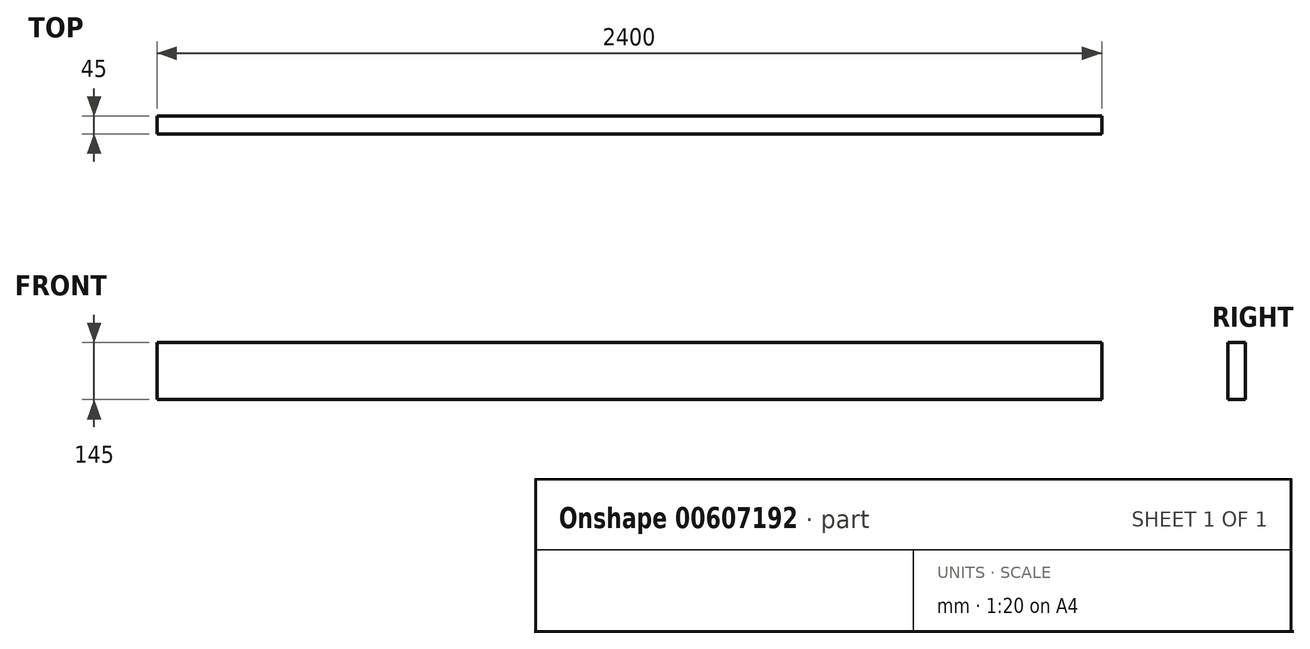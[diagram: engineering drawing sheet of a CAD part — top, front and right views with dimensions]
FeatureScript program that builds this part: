
annotation { "Feature Type Name" : "Feature", "Feature Type Description" : "" }
export const myFeature = defineFeature(function(context is Context, id is Id, definition is map)
    precondition{}
    {
        {
            var Q0;
            Q0=qCreatedBy(makeId("Front.planeOp"),FACE);
            var sketch = newSketch(context, id + "F0", { "sketchPlane" : qUnion([Q0])});
            skLineSegment(sketch, "E0.bottom", {"start": v(0, 0) * mm, "end": v(2400, 0) * mm});
            skLineSegment(sketch, "E0.top", {"start": v(0, 145) * mm, "end": v(2400, 145) * mm});
            skLineSegment(sketch, "E0.left", {"start": v(0, 0) * mm, "end": v(0, 145) * mm});
            skLineSegment(sketch, "E0.right", {"start": v(2400, 0) * mm, "end": v(2400, 145) * mm});
            skLineSegment(sketch, "E1.top", {"start": v(0, -13) * mm, "end": v(2400, -13) * mm});
            skLineSegment(sketch, "E1.left", {"start": v(0, 0) * mm, "end": v(0, -13) * mm});
            skLineSegment(sketch, "E1.right", {"start": v(2400, 0) * mm, "end": v(2400, -13) * mm});
            skLineSegment(sketch, "E2.top", {"start": v(0, -58) * mm, "end": v(2400, -58) * mm});
            skLineSegment(sketch, "E2.left", {"start": v(0, -13) * mm, "end": v(0, -58) * mm});
            skLineSegment(sketch, "E2.right", {"start": v(2400, -13) * mm, "end": v(2400, -58) * mm});
            skLineSegment(sketch, "E3.top", {"start": v(0, -76) * mm, "end": v(2400, -76) * mm});
            skLineSegment(sketch, "E3.left", {"start": v(0, -58) * mm, "end": v(0, -76) * mm});
            skLineSegment(sketch, "E3.right", {"start": v(2400, -58) * mm, "end": v(2400, -76) * mm});
            skLineSegment(sketch, "E4.bottom", {"start": v(0, 145) * mm, "end": v(145, 145) * mm});
            skLineSegment(sketch, "E4.top", {"start": v(0, 190) * mm, "end": v(145, 190) * mm});
            skLineSegment(sketch, "E4.left", {"start": v(0, 145) * mm, "end": v(0, 190) * mm});
            skLineSegment(sketch, "E4.right", {"start": v(145, 145) * mm, "end": v(145, 190) * mm});
            skLineSegment(sketch, "E5.top", {"start": v(0, 235) * mm, "end": v(145, 235) * mm});
            skLineSegment(sketch, "E5.left", {"start": v(0, 190) * mm, "end": v(0, 235) * mm});
            skLineSegment(sketch, "E5.right", {"start": v(145, 190) * mm, "end": v(145, 235) * mm});
            skLineSegment(sketch, "E6.top", {"start": v(0, 2297) * mm, "end": v(145, 2297) * mm});
            skLineSegment(sketch, "E6.left", {"start": v(0, 235) * mm, "end": v(0, 2297) * mm});
            skLineSegment(sketch, "E6.right", {"start": v(145, 235) * mm, "end": v(145, 2297) * mm});
            skLineSegment(sketch, "E7.top", {"start": v(0, 2342) * mm, "end": v(145, 2342) * mm});
            skLineSegment(sketch, "E7.left", {"start": v(0, 2297) * mm, "end": v(0, 2342) * mm});
            skLineSegment(sketch, "E7.right", {"start": v(145, 2297) * mm, "end": v(145, 2342) * mm});
            skLineSegment(sketch, "E8.top", {"start": v(0, 2387) * mm, "end": v(145, 2387) * mm});
            skLineSegment(sketch, "E8.left", {"start": v(0, 2342) * mm, "end": v(0, 2387) * mm});
            skLineSegment(sketch, "E8.right", {"start": v(145, 2342) * mm, "end": v(145, 2387) * mm});
            skLineSegment(sketch, "E9.bottom", {"start": v(2400, 145) * mm, "end": v(2255, 145) * mm});
            skLineSegment(sketch, "E9.top", {"start": v(2400, 190) * mm, "end": v(2255, 190) * mm});
            skLineSegment(sketch, "E9.left", {"start": v(2400, 145) * mm, "end": v(2400, 190) * mm});
            skLineSegment(sketch, "E9.right", {"start": v(2255, 145) * mm, "end": v(2255, 190) * mm});
            skLineSegment(sketch, "E10.bottom", {"start": v(2255, 190) * mm, "end": v(2400, 190) * mm});
            skLineSegment(sketch, "E10.top", {"start": v(2255, 3497) * mm, "end": v(2400, 3497) * mm});
            skLineSegment(sketch, "E10.left", {"start": v(2255, 190) * mm, "end": v(2255, 3497) * mm});
            skLineSegment(sketch, "E10.right", {"start": v(2400, 190) * mm, "end": v(2400, 3497) * mm});
            skLineSegment(sketch, "E11.top", {"start": v(2255, 3542) * mm, "end": v(2400, 3542) * mm});
            skLineSegment(sketch, "E11.left", {"start": v(2255, 3497) * mm, "end": v(2255, 3542) * mm});
            skLineSegment(sketch, "E11.right", {"start": v(2400, 3497) * mm, "end": v(2400, 3542) * mm});
            skLineSegment(sketch, "E12.bottom", {"start": v(2255, 3542) * mm, "end": v(2490.76, 3542) * mm});
            skLineSegment(sketch, "E12.top", {"start": v(2255, 3587) * mm, "end": v(2490.76, 3587) * mm});
            skLineSegment(sketch, "E12.left", {"start": v(2255, 3542) * mm, "end": v(2255, 3587) * mm});
            skLineSegment(sketch, "E12.right", {"start": v(2490.76, 3542) * mm, "end": v(2490.76, 3587) * mm});
            skLineSegment(sketch, "E13", {"start": v(0, 2387) * mm, "end": v(0, 2467) * mm});
            skLineSegment(sketch, "E14", {"start": v(0, 2467) * mm, "end": v(2490.76, 3712.38) * mm});
            skLineSegment(sketch, "E15", {"start": v(145, 2377.38) * mm, "end": v(2490.76, 3550.26) * mm});
            skSolve(sketch);
        }
        {
            var Q0;
            Q0=makeQuery(id+"F0.imprint","IMPRINT",FACE,{"disambiguationData":[TD([[makeQuery(id+"F0.imprint","IMPRINT",EDGE,{"derivedFrom":sQuery(id+"F0.wireOp",EDGE,"E0.top")}),-1.0]])]});
            extrude(context, id + "F1", {"entities" : qUnion([Q0]), "depth" : 45 * mm, "offsetDistance" : 25 * mm});
        }
    });
